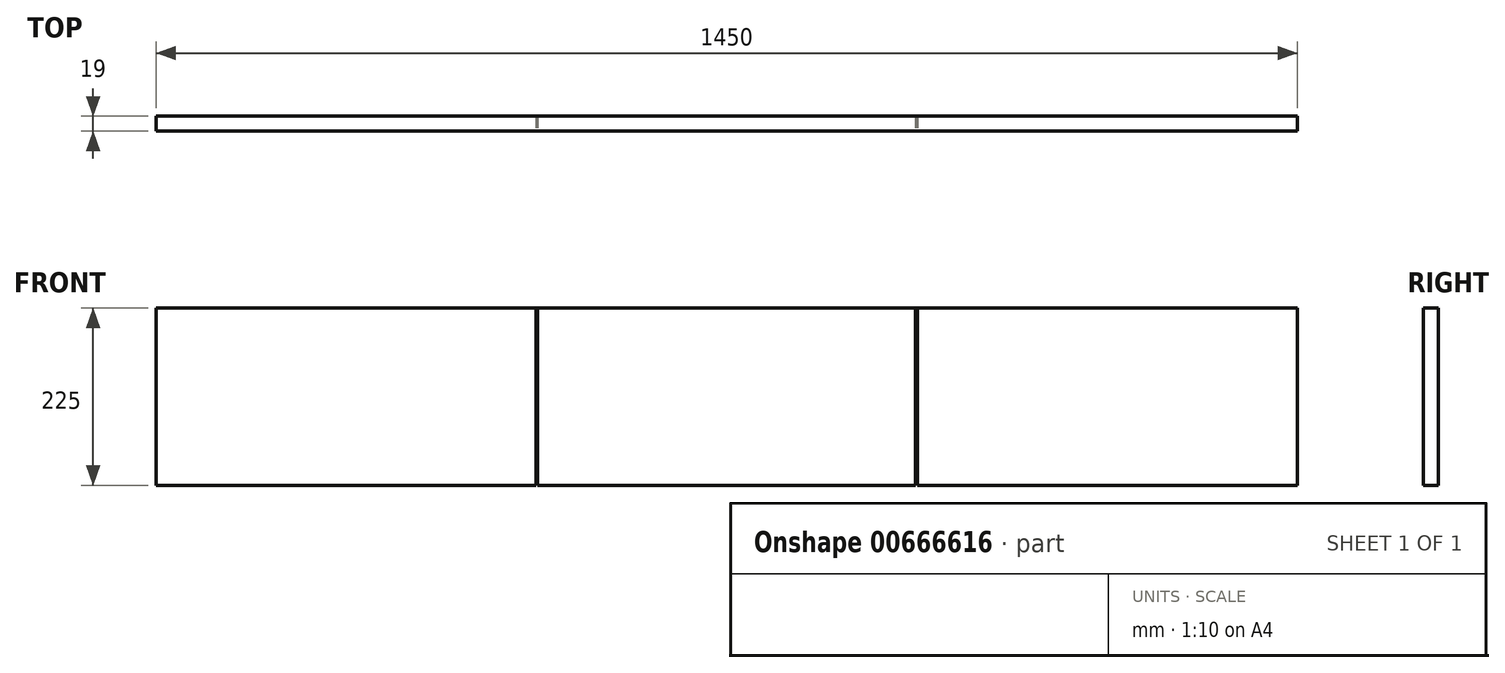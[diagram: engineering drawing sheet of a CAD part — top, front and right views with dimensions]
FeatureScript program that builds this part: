
annotation { "Feature Type Name" : "Feature", "Feature Type Description" : "" }
export const myFeature = defineFeature(function(context is Context, id is Id, definition is map)
    precondition{}
    {
        {
            var Q0;
            Q0=qCreatedBy(makeId("Front.planeOp"),FACE);
            var sketch = newSketch(context, id + "F0", { "sketchPlane" : qUnion([Q0])});
            skLineSegment(sketch, "E0.bottom", {"start": v(0, 0) * mm, "end": v(-1450, 0) * mm});
            skLineSegment(sketch, "E0.top", {"start": v(0, 225) * mm, "end": v(-1450, 225) * mm});
            skLineSegment(sketch, "E0.left", {"start": v(0, 0) * mm, "end": v(0, 225) * mm});
            skLineSegment(sketch, "E0.right", {"start": v(-1450, 0) * mm, "end": v(-1450, 225) * mm});
            skLineSegment(sketch, "E1", {"start": v(0, 0) * mm, "end": v(-1450, 0) * mm, "construction": true});
            skLineSegment(sketch, "E2", {"start": v(-1450, 0) * mm, "end": v(-967, 0) * mm, "construction": true});
            skLineSegment(sketch, "E3", {"start": v(0, 0) * mm, "end": v(-483, 0) * mm, "construction": true});
            skLineSegment(sketch, "E4.bottom", {"start": v(-483, 0) * mm, "end": v(-485, 0) * mm});
            skLineSegment(sketch, "E4.top", {"start": v(-483, 224) * mm, "end": v(-485, 224) * mm});
            skLineSegment(sketch, "E4.left", {"start": v(-483, 0) * mm, "end": v(-483, 224) * mm});
            skLineSegment(sketch, "E4.right", {"start": v(-485, 0) * mm, "end": v(-485, 224) * mm});
            skLineSegment(sketch, "E5.bottom", {"start": v(-967, 0) * mm, "end": v(-965, 0) * mm});
            skLineSegment(sketch, "E5.top", {"start": v(-967, 224) * mm, "end": v(-965, 224) * mm});
            skLineSegment(sketch, "E5.left", {"start": v(-967, 0) * mm, "end": v(-967, 224) * mm});
            skLineSegment(sketch, "E5.right", {"start": v(-965, 0) * mm, "end": v(-965, 224) * mm});
            skSolve(sketch);
        }
        {
            var Q0;
            Q0=makeQuery(id+"F0.imprint","IMPRINT",FACE,{"disambiguationData":[TD([[makeQuery(id+"F0.imprint","IMPRINT",EDGE,{"derivedFrom":sQuery(id+"F0.wireOp",EDGE,"E0.top")}),1.0]])]});
            var Q1;
            Q1=sQuery(id+"F0.wireOp",EDGE,"E0.top");
            var Q2;
            Q2=sQuery(id+"F0.wireOp",EDGE,"E0.right");
            var Q3;
            Q3=sQuery(id+"F0.wireOp",EDGE,"E0.bottom");
            var Q4;
            Q4=sQuery(id+"F0.wireOp",EDGE,"E0.left");
            extrude(context, id + "F1", {"entities" : qUnion([Q0]), "surfaceEntities" : qUnion([Q1, Q2, Q3, Q4]), "oppositeDirection" : true, "depth" : 19 * mm, "offsetDistance" : 25 * mm});
        }
    });
